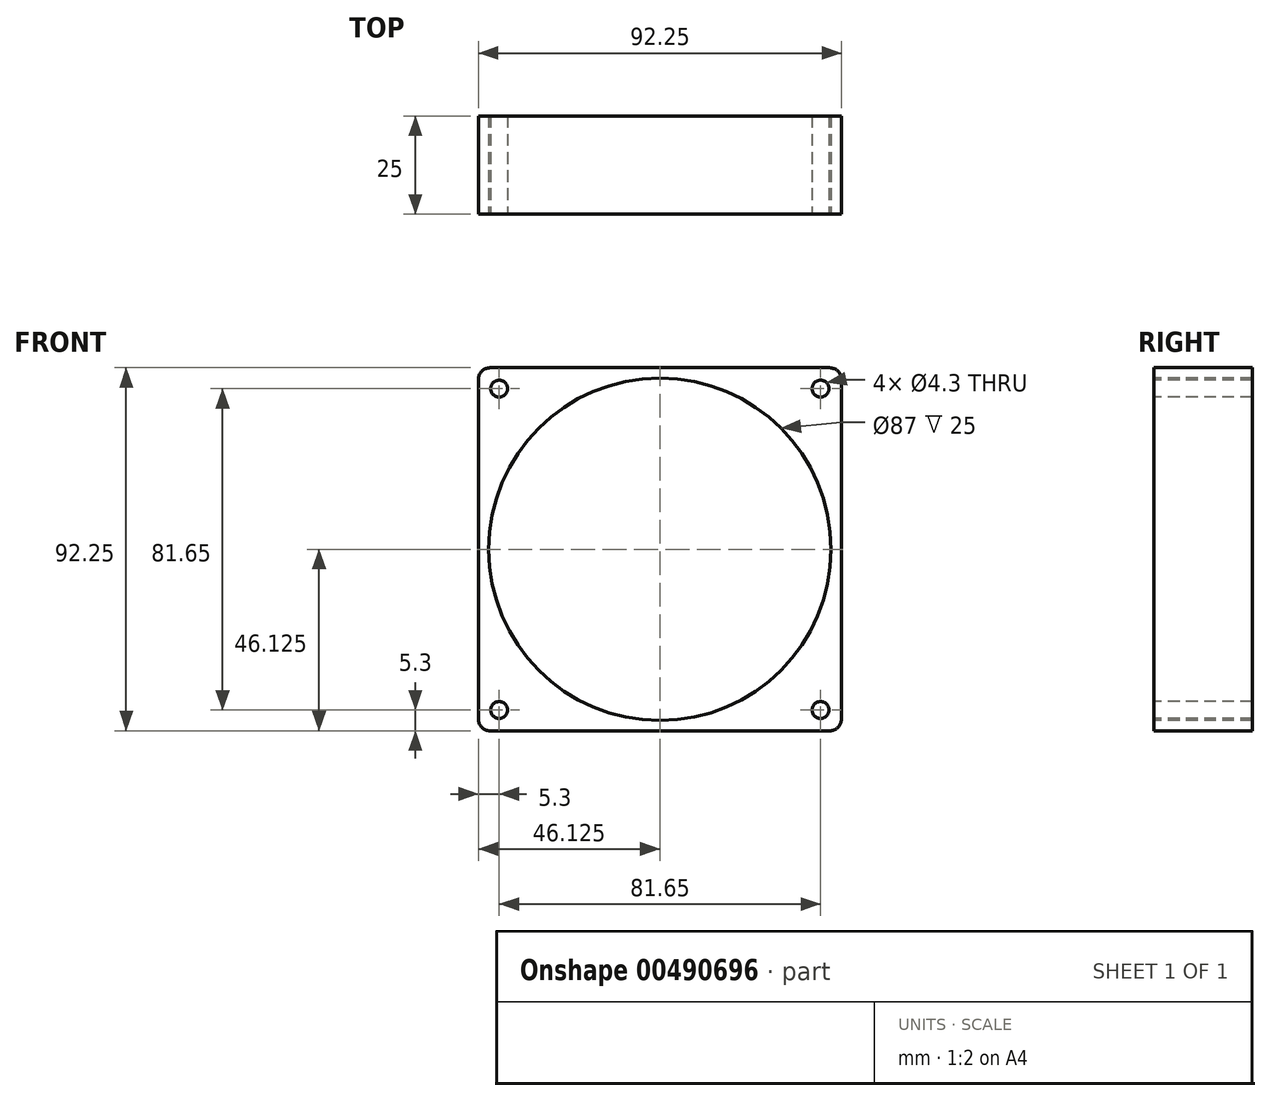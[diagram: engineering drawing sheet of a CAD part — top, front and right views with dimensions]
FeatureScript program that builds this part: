
annotation { "Feature Type Name" : "Feature", "Feature Type Description" : "" }
export const myFeature = defineFeature(function(context is Context, id is Id, definition is map)
    precondition{}
    {
        {
            var Q0;
            Q0=qCreatedBy(makeId("Front.planeOp"),FACE);
            var sketch = newSketch(context, id + "F0", { "sketchPlane" : qUnion([Q0])});
            skLineSegment(sketch, "E0.bottom", {"start": v(0, 0) * mm, "end": v(92.25, 0) * mm});
            skLineSegment(sketch, "E0.top", {"start": v(0, 92.25) * mm, "end": v(92.25, 92.25) * mm});
            skLineSegment(sketch, "E0.left", {"start": v(0, 0) * mm, "end": v(0, 92.25) * mm});
            skLineSegment(sketch, "E0.right", {"start": v(92.25, 0) * mm, "end": v(92.25, 92.25) * mm});
            skSolve(sketch);
        }
        {
            var Q0;
            Q0 = qSketchRegion(id + "F0", true);
            extrude(context, id + "F1", {"entities" : qUnion([Q0]), "depth" : 25 * mm});
        }
        {
            var Q0;
            Q0=makeQuery(id+"F1.opExtrude","CAP_FACE",FACE,{"disambiguationData":[OSD([sQuery(id+"F0.wireOp",EDGE,"E0.bottom"),sQuery(id+"F0.wireOp",EDGE,"E0.top"),sQuery(id+"F0.wireOp",EDGE,"E0.left"),sQuery(id+"F0.wireOp",EDGE,"E0.right")])],"isStart":false});
            var sketch = newSketch(context, id + "F2", { "sketchPlane" : qUnion([Q0])});
            skCircle(sketch, "E1", {"center": v(46.12, 46.12) * mm, "radius": 43.5 * mm});
            skPoint(sketch, "E1.centerSnap0", {"position": v(46.12, 92.25) * mm});
            skPoint(sketch, "E1.centerSnap1", {"position": v(0, 46.12) * mm});
            skSolve(sketch);
        }
        {
            var Q0;
            Q0 = qSketchRegion(id + "F2", true);
            extrude(context, id + "F3", {"entities" : qUnion([Q0]), "operationType" : NewBodyOperationType.REMOVE, "endBound" : BoundingType.THROUGH_ALL, "oppositeDirection" : true, "depth" : 25 * mm});
        }
        {
            var Q0;
            Q0=makeQuery(id+"F1.opExtrude","CAP_FACE",FACE,{"disambiguationData":[OSD([sQuery(id+"F0.wireOp",EDGE,"E0.bottom"),sQuery(id+"F0.wireOp",EDGE,"E0.top"),sQuery(id+"F0.wireOp",EDGE,"E0.left"),sQuery(id+"F0.wireOp",EDGE,"E0.right")])],"isStart":false});
            var sketch = newSketch(context, id + "F4", { "sketchPlane" : qUnion([Q0])});
            skPoint(sketch, "E2", {"position": v(5.3, 86.95) * mm});
            skPoint(sketch, "E3", {"position": v(5.3, 5.3) * mm});
            skLineSegment(sketch, "E4", {"start": v(46.12, 92.25) * mm, "end": v(46.12, 0) * mm, "construction": true});
            skPoint(sketch, "E5.MirrorP", {"position": v(86.95, 86.95) * mm});
            skPoint(sketch, "E6.MirrorP", {"position": v(86.95, 5.3) * mm});
            skSolve(sketch);
        }
        {
            var Q0;
            Q0=sQuery(id+"F4.wireOp",VERTEX,"E2");
            var Q1;
            Q1=sQuery(id+"F4.wireOp",VERTEX,"E3");
            var Q2;
            Q2=sQuery(id+"F4.wireOp",VERTEX,"E6.MirrorP");
            var Q3;
            Q3=sQuery(id+"F4.wireOp",VERTEX,"E5.MirrorP");
            var Q4;
            Q4=makeQuery(id+"F1.opExtrude","SWEPT_BODY",BODY,{"disambiguationData":[OSD([sQuery(id+"F0.wireOp",EDGE,"E0.bottom"),sQuery(id+"F0.wireOp",EDGE,"E0.top"),sQuery(id+"F0.wireOp",EDGE,"E0.left"),sQuery(id+"F0.wireOp",EDGE,"E0.right")])]});
            hole(context, id + "F5", {"style" : HoleStyle.SIMPLE, "endStyle" : HoleEndStyle.THROUGH, "holeDiameter" : 4.3 * mm, "isTappedThrough" : true, "tappedDepth" : 12 * mm, "tapClearance" : 3, "locations" : qUnion([Q0, Q1, Q2, Q3]), "scope" : qUnion([Q4])});
        }
        {
            var Q0;
            Q0=makeQuery(id+"F1.opExtrude","SWEPT_EDGE",EDGE,{"disambiguationData":[OSD([sQuery(id+"F0.wireOp",EDGE,"E0.top"),sQuery(id+"F0.wireOp",EDGE,"E0.right")])]});
            var Q1;
            Q1=makeQuery(id+"F1.opExtrude","SWEPT_EDGE",EDGE,{"disambiguationData":[OSD([sQuery(id+"F0.wireOp",EDGE,"E0.top"),sQuery(id+"F0.wireOp",EDGE,"E0.left")])]});
            var Q2;
            Q2=makeQuery(id+"F1.opExtrude","SWEPT_EDGE",EDGE,{"disambiguationData":[OSD([sQuery(id+"F0.wireOp",EDGE,"E0.bottom"),sQuery(id+"F0.wireOp",EDGE,"E0.left")])]});
            var Q3;
            Q3=makeQuery(id+"F1.opExtrude","SWEPT_EDGE",EDGE,{"disambiguationData":[OSD([sQuery(id+"F0.wireOp",EDGE,"E0.bottom"),sQuery(id+"F0.wireOp",EDGE,"E0.right")])]});
            fillet(context, id + "F6", {"entities" : qUnion([Q0, Q1, Q2, Q3]), "radius" : 3 * mm, "tangentPropagation" : true, "allowEdgeOverflow" : false});
        }
    });
